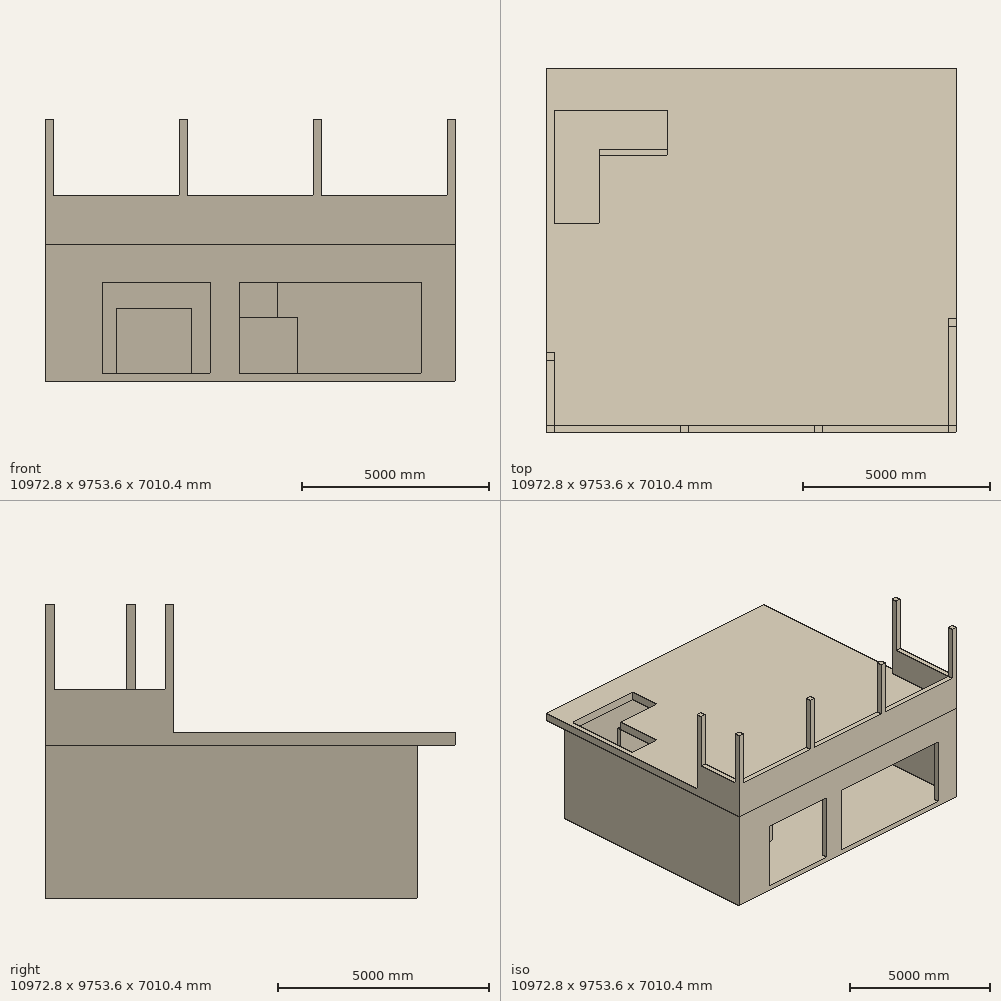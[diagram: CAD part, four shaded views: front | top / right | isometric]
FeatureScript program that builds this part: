
annotation { "Feature Type Name" : "Feature", "Feature Type Description" : "" }
export const myFeature = defineFeature(function(context is Context, id is Id, definition is map)
    precondition{}
    {
        {
            var Q0;
            Q0=qCreatedBy(makeId("Top.planeOp"),FACE);
            var sketch = newSketch(context, id + "F0", { "sketchPlane" : qUnion([Q0])});
            skLineSegment(sketch, "E0.bottom", {"start": v(0, 0) * mm, "end": v(10972.8, 0) * mm});
            skLineSegment(sketch, "E0.top", {"start": v(0, -8839.2) * mm, "end": v(10972.8, -8839.2) * mm});
            skLineSegment(sketch, "E0.left", {"start": v(0, 0) * mm, "end": v(0, -8839.2) * mm});
            skLineSegment(sketch, "E0.right", {"start": v(10972.8, 0) * mm, "end": v(10972.8, -8839.2) * mm});
            skSolve(sketch);
        }
        {
            var Q0;
            Q0=qSketchRegion(id+"F0",true);
            extrude(context, id + "F1", {"entities" : qUnion([Q0]), "depth" : 3657.6 * mm});
        }
        {
            var Q0;
            Q0=makeQuery(id+"F1.opExtrude","CAP_FACE",FACE,{"disambiguationData":[OSD([sQuery(id+"F0.wireOp",EDGE,"E0.bottom"),sQuery(id+"F0.wireOp",EDGE,"E0.top"),sQuery(id+"F0.wireOp",EDGE,"E0.left"),sQuery(id+"F0.wireOp",EDGE,"E0.right")])],"isStart":false});
            shell(context, id + "F2", {"entities" : qUnion([Q0]), "thickness" : 203.2 * mm});
        }
        {
            var Q0;
            Q0=makeQuery(id+"F1.opExtrude","SWEPT_FACE",FACE,{"disambiguationData":[OSD([sQuery(id+"F0.wireOp",EDGE,"E0.top")])]});
            var sketch = newSketch(context, id + "F3", { "sketchPlane" : qUnion([Q0])});
            skLineSegment(sketch, "E1.bottom", {"start": v(1524, 2641.6) * mm, "end": v(4419.6, 2641.6) * mm});
            skLineSegment(sketch, "E1.top", {"start": v(1524, 203.2) * mm, "end": v(4419.6, 203.2) * mm});
            skLineSegment(sketch, "E1.left", {"start": v(1524, 2641.6) * mm, "end": v(1524, 203.2) * mm});
            skLineSegment(sketch, "E1.right", {"start": v(4419.6, 2641.6) * mm, "end": v(4419.6, 203.2) * mm});
            skLineSegment(sketch, "E2.bottom", {"start": v(5181.6, 2641.6) * mm, "end": v(10058.4, 2641.6) * mm});
            skLineSegment(sketch, "E2.top", {"start": v(5181.6, 203.2) * mm, "end": v(10058.4, 203.2) * mm});
            skLineSegment(sketch, "E2.left", {"start": v(5181.6, 2641.6) * mm, "end": v(5181.6, 203.2) * mm});
            skLineSegment(sketch, "E2.right", {"start": v(10058.4, 2641.6) * mm, "end": v(10058.4, 203.2) * mm});
            skSolve(sketch);
        }
        {
            var Q0;
            Q0=qSketchRegion(id+"F3",true);
            var Q1;
            Q1=makeQuery(id+"F2.opShell","OFFSET_FACE",FACE,{"disambiguationData":[OSD([sQuery(id+"F0.wireOp",EDGE,"E0.top")])]});
            extrude(context, id + "F4", {"entities" : qUnion([Q0]), "operationType" : NewBodyOperationType.REMOVE, "endBound" : BoundingType.UP_TO_SURFACE, "oppositeDirection" : true, "endBoundEntityFace" : qUnion([Q1]), "depth" : 25.4 * mm});
        }
        {
            var Q0;
            Q0=makeQuery(id+"F4.boolean.opBoolean","MERGE",FACE,{"derivedFrom":[makeQuery(id+"F2.opShell","OFFSET_FACE",FACE,{"disambiguationData":[OSD([sQuery(id+"F0.wireOp",EDGE,"E0.bottom"),sQuery(id+"F0.wireOp",EDGE,"E0.top"),sQuery(id+"F0.wireOp",EDGE,"E0.left"),sQuery(id+"F0.wireOp",EDGE,"E0.right")])]}),makeQuery(id+"F4.opExtrude","SWEPT_FACE",FACE,{"disambiguationData":[OSD([sQuery(id+"F3.wireOp",EDGE,"E1.top")])]}),makeQuery(id+"F4.opExtrude","SWEPT_FACE",FACE,{"disambiguationData":[OSD([sQuery(id+"F3.wireOp",EDGE,"E2.top")])]})]});
            var sketch = newSketch(context, id + "F5", { "sketchPlane" : qUnion([Q0])});
            skLineSegment(sketch, "E3.bottom", {"start": v(1891.23, -1512.12) * mm, "end": v(3897.83, -1512.12) * mm});
            skLineSegment(sketch, "E3.top", {"start": v(1891.23, -6617.52) * mm, "end": v(3897.83, -6617.52) * mm});
            skLineSegment(sketch, "E3.left", {"start": v(1891.23, -1512.12) * mm, "end": v(1891.23, -6617.52) * mm});
            skLineSegment(sketch, "E3.right", {"start": v(3897.83, -1512.12) * mm, "end": v(3897.83, -6617.52) * mm});
            skSolve(sketch);
        }
        {
            var Q0;
            Q0 = qSketchRegion(id + "F5", true);
            extrude(context, id + "F6", {"entities" : qUnion([Q0]), "depth" : 1752.6 * mm});
        }
        {
            var Q0;
            Q0=makeQuery(id+"F4.boolean.opBoolean","MERGE",FACE,{"derivedFrom":[makeQuery(id+"F2.opShell","OFFSET_FACE",FACE,{"disambiguationData":[OSD([sQuery(id+"F0.wireOp",EDGE,"E0.bottom"),sQuery(id+"F0.wireOp",EDGE,"E0.top"),sQuery(id+"F0.wireOp",EDGE,"E0.left"),sQuery(id+"F0.wireOp",EDGE,"E0.right")])]}),makeQuery(id+"F4.opExtrude","SWEPT_FACE",FACE,{"disambiguationData":[OSD([sQuery(id+"F3.wireOp",EDGE,"E1.top")])]}),makeQuery(id+"F4.opExtrude","SWEPT_FACE",FACE,{"disambiguationData":[OSD([sQuery(id+"F3.wireOp",EDGE,"E2.top")])]})]});
            var sketch = newSketch(context, id + "F7", { "sketchPlane" : qUnion([Q0])});
            skLineSegment(sketch, "E4.bottom", {"start": v(5045.4, -1753.86) * mm, "end": v(6747.2, -1753.86) * mm});
            skLineSegment(sketch, "E4.top", {"start": v(5045.4, -5665.46) * mm, "end": v(6747.2, -5665.46) * mm});
            skLineSegment(sketch, "E4.left", {"start": v(5045.4, -1753.86) * mm, "end": v(5045.4, -5665.46) * mm});
            skLineSegment(sketch, "E4.right", {"start": v(6747.2, -1753.86) * mm, "end": v(6747.2, -5665.46) * mm});
            skSolve(sketch);
        }
        {
            var Q0;
            Q0=makeQuery(id+"F7.imprint","IMPRINT",FACE,{"disambiguationData":[TD([[makeQuery(id+"F7.imprint","IMPRINT",EDGE,{"derivedFrom":sQuery(id+"F7.wireOp",EDGE,"E4.bottom")}),-1.0]])]});
            extrude(context, id + "F8", {"entities" : qUnion([Q0]), "depth" : 1498.6 * mm});
        }
        {
            var Q0;
            Q0=makeQuery(id+"F4.boolean.opBoolean","MERGE",FACE,{"derivedFrom":[makeQuery(id+"F2.opShell","OFFSET_FACE",FACE,{"disambiguationData":[OSD([sQuery(id+"F0.wireOp",EDGE,"E0.bottom"),sQuery(id+"F0.wireOp",EDGE,"E0.top"),sQuery(id+"F0.wireOp",EDGE,"E0.left"),sQuery(id+"F0.wireOp",EDGE,"E0.right")])]}),makeQuery(id+"F4.opExtrude","SWEPT_FACE",FACE,{"disambiguationData":[OSD([sQuery(id+"F3.wireOp",EDGE,"E1.top")])]}),makeQuery(id+"F4.opExtrude","SWEPT_FACE",FACE,{"disambiguationData":[OSD([sQuery(id+"F3.wireOp",EDGE,"E2.top")])]})]});
            var sketch = newSketch(context, id + "F9", { "sketchPlane" : qUnion([Q0])});
            skLineSegment(sketch, "E5", {"start": v(6197.6, -203.2) * mm, "end": v(6197.6, -1422.4) * mm});
            skLineSegment(sketch, "E6", {"start": v(6197.6, -1422.4) * mm, "end": v(1422.4, -1422.4) * mm});
            skLineSegment(sketch, "E7", {"start": v(1422.4, -1270) * mm, "end": v(6045.2, -1270) * mm});
            skLineSegment(sketch, "E8", {"start": v(6045.2, -1270) * mm, "end": v(6045.2, -203.2) * mm});
            skLineSegment(sketch, "E9", {"start": v(6045.2, -203.2) * mm, "end": v(6197.6, -203.2) * mm});
            skLineSegment(sketch, "E10", {"start": v(1422.4, -1270) * mm, "end": v(1422.4, -1422.4) * mm});
            skSolve(sketch);
        }
        {
            var Q0;
            Q0 = qSketchRegion(id + "F9", true);
            var Q1;
            Q1=makeQuery(id+"F1.opExtrude","CAP_FACE",FACE,{"disambiguationData":[OSD([sQuery(id+"F0.wireOp",EDGE,"E0.bottom"),sQuery(id+"F0.wireOp",EDGE,"E0.top"),sQuery(id+"F0.wireOp",EDGE,"E0.left"),sQuery(id+"F0.wireOp",EDGE,"E0.right")])],"isStart":false});
            extrude(context, id + "F10", {"entities" : qUnion([Q0]), "operationType" : NewBodyOperationType.ADD, "endBound" : BoundingType.UP_TO_SURFACE, "endBoundEntityFace" : qUnion([Q1]), "depth" : 25.4 * mm});
        }
        {
            var Q0;
            {var subQ0=sQuery(id+"F0.wireOp",EDGE,"E0.right");var subQ1=sQuery(id+"F0.wireOp",EDGE,"E0.left");var subQ2=sQuery(id+"F0.wireOp",EDGE,"E0.top");var subQ3=sQuery(id+"F0.wireOp",EDGE,"E0.bottom");Q0=makeQuery(id+"F10.boolean.opBoolean","MERGE",FACE,{"derivedFrom":[makeQuery(id+"F1.opExtrude","CAP_FACE",FACE,{"disambiguationData":[OSD([subQ3,subQ2,subQ1,subQ0])],"isStart":false}),makeQuery(id+"F10.opExtrude","CAP_FACE",FACE,{"disambiguationData":[OSD([subQ3,subQ2,subQ1,subQ0])],"isStart":false})]});}
            var sketch = newSketch(context, id + "F11", { "sketchPlane" : qUnion([Q0])});
            skLineSegment(sketch, "E11.bottom", {"start": v(0, -8839.2) * mm, "end": v(10972.8, -8839.2) * mm});
            skLineSegment(sketch, "E11.top", {"start": v(0, 914.4) * mm, "end": v(10972.8, 914.4) * mm});
            skLineSegment(sketch, "E11.left", {"start": v(0, -8839.2) * mm, "end": v(0, 914.4) * mm});
            skLineSegment(sketch, "E11.right", {"start": v(10972.8, -8839.2) * mm, "end": v(10972.8, 914.4) * mm});
            skSolve(sketch);
        }
        {
            var Q0;
            Q0 = qSketchRegion(id + "F11", true);
            extrude(context, id + "F12", {"entities" : qUnion([Q0]), "depth" : 304.8 * mm});
        }
        {
            var Q0;
            Q0=makeQuery(id+"F12.opExtrude","CAP_FACE",FACE,{"disambiguationData":[OSD([sQuery(id+"F11.wireOp",EDGE,"E11.bottom"),sQuery(id+"F11.wireOp",EDGE,"E11.top"),sQuery(id+"F11.wireOp",EDGE,"E11.left"),sQuery(id+"F11.wireOp",EDGE,"E11.right")])],"isStart":false});
            var sketch = newSketch(context, id + "F13", { "sketchPlane" : qUnion([Q0])});
            skLineSegment(sketch, "E12", {"start": v(10769.6, -5791.2) * mm, "end": v(10972.8, -5791.2) * mm});
            skLineSegment(sketch, "E13", {"start": v(10972.8, -5791.2) * mm, "end": v(10972.8, -8839.2) * mm});
            skLineSegment(sketch, "E14", {"start": v(10972.8, -8839.2) * mm, "end": v(0, -8839.2) * mm});
            skLineSegment(sketch, "E15", {"start": v(0, -8839.2) * mm, "end": v(0, -6705.6) * mm});
            skLineSegment(sketch, "E16", {"start": v(0, -6705.6) * mm, "end": v(203.2, -6705.6) * mm});
            skLineSegment(sketch, "E17", {"start": v(203.2, -6705.6) * mm, "end": v(203.2, -8636) * mm});
            skLineSegment(sketch, "E18", {"start": v(203.2, -8636) * mm, "end": v(10769.6, -8636) * mm});
            skLineSegment(sketch, "E19", {"start": v(10769.6, -8636) * mm, "end": v(10769.6, -5791.2) * mm});
            skSolve(sketch);
        }
        {
            var Q0;
            Q0 = qSketchRegion(id + "F13", true);
            extrude(context, id + "F14", {"entities" : qUnion([Q0]), "operationType" : NewBodyOperationType.ADD, "depth" : 1016 * mm});
        }
        {
            var Q0;
            Q0=makeQuery(id+"F14.opExtrude","CAP_FACE",FACE,{"disambiguationData":[OSD([sQuery(id+"F13.wireOp",EDGE,"E12"),sQuery(id+"F13.wireOp",EDGE,"E13"),sQuery(id+"F13.wireOp",EDGE,"E14"),sQuery(id+"F13.wireOp",EDGE,"E15"),sQuery(id+"F13.wireOp",EDGE,"E16"),sQuery(id+"F13.wireOp",EDGE,"E17"),sQuery(id+"F13.wireOp",EDGE,"E18"),sQuery(id+"F13.wireOp",EDGE,"E19")])],"isStart":false});
            var sketch = newSketch(context, id + "F15", { "sketchPlane" : qUnion([Q0])});
            skLineSegment(sketch, "E20.bottom", {"start": v(203.2, -8636) * mm, "end": v(0, -8636) * mm});
            skLineSegment(sketch, "E20.top", {"start": v(203.2, -8839.2) * mm, "end": v(0, -8839.2) * mm});
            skLineSegment(sketch, "E20.left", {"start": v(203.2, -8636) * mm, "end": v(203.2, -8839.2) * mm});
            skLineSegment(sketch, "E20.right", {"start": v(0, -8636) * mm, "end": v(0, -8839.2) * mm});
            skLineSegment(sketch, "E21.bottom", {"start": v(10769.6, -8636) * mm, "end": v(10972.8, -8636) * mm});
            skLineSegment(sketch, "E21.top", {"start": v(10769.6, -8839.2) * mm, "end": v(10972.8, -8839.2) * mm});
            skLineSegment(sketch, "E21.left", {"start": v(10769.6, -8636) * mm, "end": v(10769.6, -8839.2) * mm});
            skLineSegment(sketch, "E21.right", {"start": v(10972.8, -8636) * mm, "end": v(10972.8, -8839.2) * mm});
            skLineSegment(sketch, "E22.bottom", {"start": v(3589.87, -8636) * mm, "end": v(3793.07, -8636) * mm});
            skLineSegment(sketch, "E22.top", {"start": v(3589.87, -8839.2) * mm, "end": v(3793.07, -8839.2) * mm});
            skLineSegment(sketch, "E22.left", {"start": v(3589.87, -8636) * mm, "end": v(3589.87, -8839.2) * mm});
            skLineSegment(sketch, "E22.right", {"start": v(3793.07, -8636) * mm, "end": v(3793.07, -8839.2) * mm});
            skLineSegment(sketch, "E23.bottom", {"start": v(7179.73, -8636) * mm, "end": v(7382.93, -8636) * mm});
            skLineSegment(sketch, "E23.top", {"start": v(7179.73, -8839.2) * mm, "end": v(7382.93, -8839.2) * mm});
            skLineSegment(sketch, "E23.left", {"start": v(7179.73, -8636) * mm, "end": v(7179.73, -8839.2) * mm});
            skLineSegment(sketch, "E23.right", {"start": v(7382.93, -8636) * mm, "end": v(7382.93, -8839.2) * mm});
            skLineSegment(sketch, "E24", {"start": v(203.2, -8839.2) * mm, "end": v(3589.87, -8839.2) * mm, "construction": true});
            skLineSegment(sketch, "E25", {"start": v(3793.07, -8839.2) * mm, "end": v(7179.73, -8839.2) * mm, "construction": true});
            skLineSegment(sketch, "E26", {"start": v(7382.93, -8839.2) * mm, "end": v(10769.6, -8839.2) * mm, "construction": true});
            skLineSegment(sketch, "E27.bottom", {"start": v(0, -6705.6) * mm, "end": v(203.2, -6705.6) * mm});
            skLineSegment(sketch, "E27.top", {"start": v(0, -6908.8) * mm, "end": v(203.2, -6908.8) * mm});
            skLineSegment(sketch, "E27.left", {"start": v(0, -6705.6) * mm, "end": v(0, -6908.8) * mm});
            skLineSegment(sketch, "E27.right", {"start": v(203.2, -6705.6) * mm, "end": v(203.2, -6908.8) * mm});
            skLineSegment(sketch, "E28.bottom", {"start": v(10972.8, -5791.2) * mm, "end": v(10769.6, -5791.2) * mm});
            skLineSegment(sketch, "E28.top", {"start": v(10972.8, -5994.4) * mm, "end": v(10769.6, -5994.4) * mm});
            skLineSegment(sketch, "E28.left", {"start": v(10972.8, -5791.2) * mm, "end": v(10972.8, -5994.4) * mm});
            skLineSegment(sketch, "E28.right", {"start": v(10769.6, -5791.2) * mm, "end": v(10769.6, -5994.4) * mm});
            skSolve(sketch);
        }
        {
            var Q0;
            Q0 = qSketchRegion(id + "F15", true);
            extrude(context, id + "F16", {"entities" : qUnion([Q0]), "operationType" : NewBodyOperationType.ADD, "depth" : 2032 * mm});
        }
        {
            var Q0;
            Q0=makeQuery(id+"F12.opExtrude","CAP_FACE",FACE,{"disambiguationData":[OSD([sQuery(id+"F11.wireOp",EDGE,"E11.bottom"),sQuery(id+"F11.wireOp",EDGE,"E11.top"),sQuery(id+"F11.wireOp",EDGE,"E11.left"),sQuery(id+"F11.wireOp",EDGE,"E11.right")])],"isStart":false});
            var sketch = newSketch(context, id + "F17", { "sketchPlane" : qUnion([Q0])});
            skLineSegment(sketch, "E29", {"start": v(203.2, -203.2) * mm, "end": v(203.2, -3251.2) * mm});
            skLineSegment(sketch, "E30", {"start": v(203.2, -3251.2) * mm, "end": v(1422.4, -3251.2) * mm});
            skLineSegment(sketch, "E31", {"start": v(1422.4, -3251.2) * mm, "end": v(1422.4, -1422.4) * mm});
            skLineSegment(sketch, "E32", {"start": v(1422.4, -1422.4) * mm, "end": v(3251.2, -1422.4) * mm});
            skLineSegment(sketch, "E33", {"start": v(3251.2, -1422.4) * mm, "end": v(3251.2, -203.2) * mm});
            skLineSegment(sketch, "E34", {"start": v(3251.2, -203.2) * mm, "end": v(203.2, -203.2) * mm});
            skSolve(sketch);
        }
        {
            var Q0;
            Q0 = qSketchRegion(id + "F17", true);
            extrude(context, id + "F18", {"entities" : qUnion([Q0]), "operationType" : NewBodyOperationType.REMOVE, "endBound" : BoundingType.UP_TO_NEXT, "oppositeDirection" : true, "depth" : 25.4 * mm});
        }
    });
